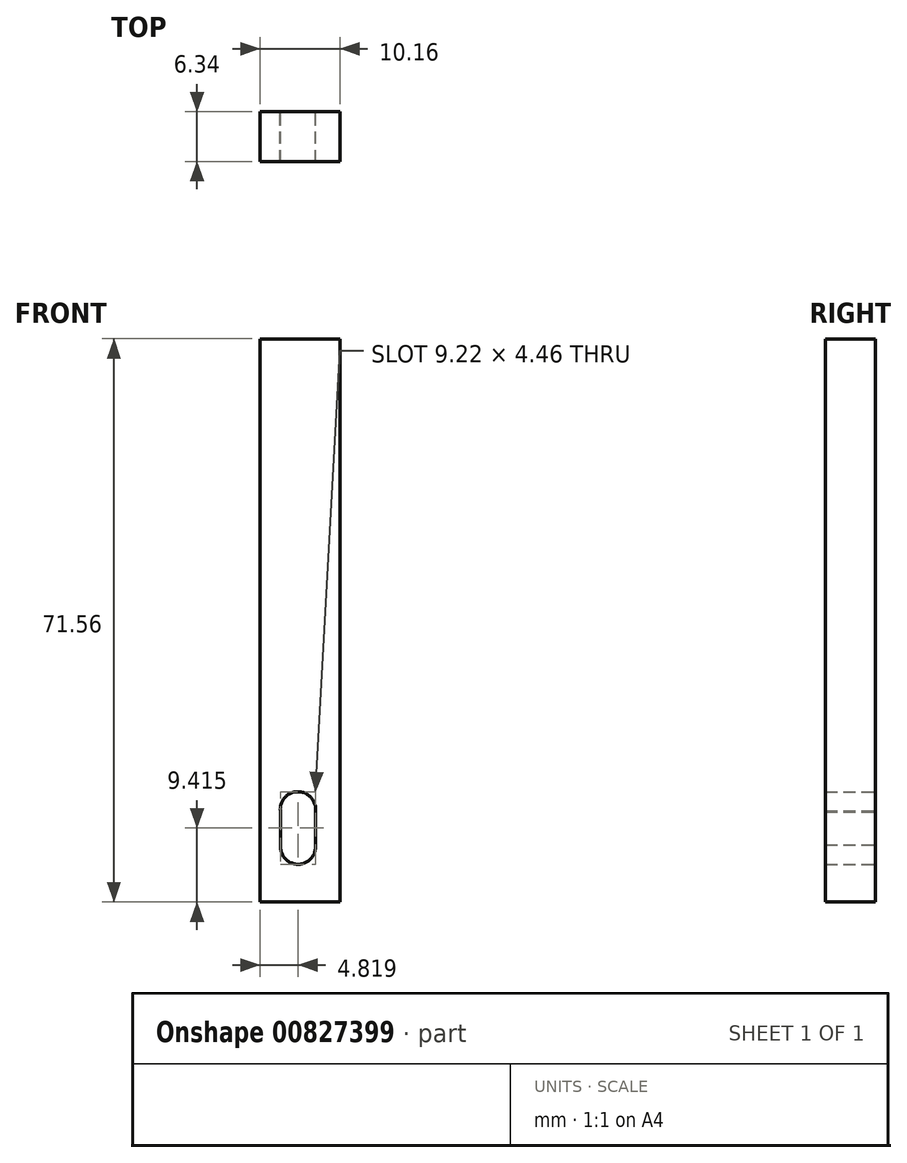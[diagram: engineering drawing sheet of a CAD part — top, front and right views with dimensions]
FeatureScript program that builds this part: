
annotation { "Feature Type Name" : "Feature", "Feature Type Description" : "" }
export const myFeature = defineFeature(function(context is Context, id is Id, definition is map)
    precondition{}
    {
        {
            var Q0;
            Q0=qCreatedBy(makeId("Front.planeOp"),FACE);
            var sketch = newSketch(context, id + "F0", { "sketchPlane" : qUnion([Q0])});
            skLineSegment(sketch, "E0.bottom", {"start": v(-5.08, 35.78) * mm, "end": v(5.08, 35.78) * mm});
            skLineSegment(sketch, "E0.top", {"start": v(-5.08, -35.78) * mm, "end": v(5.08, -35.78) * mm});
            skLineSegment(sketch, "E0.left", {"start": v(-5.08, 35.78) * mm, "end": v(-5.08, -35.78) * mm});
            skLineSegment(sketch, "E0.right", {"start": v(5.08, 35.78) * mm, "end": v(5.08, -35.78) * mm});
            skPoint(sketch, "E0.middle", {"position": v(0, 0) * mm});
            skArc(sketch, "E1", {"start": v(1.97, -24.22) * mm, "mid": v(-0.3, -21.76) * mm, "end": v(-2.49, -24.3) * mm});
            skLineSegment(sketch, "E2", {"start": v(-2.49, -24.3) * mm, "end": v(-2.49, -28.74) * mm});
            skLineSegment(sketch, "E3", {"start": v(1.97, -24.22) * mm, "end": v(1.97, -28.55) * mm});
            skArc(sketch, "E4", {"start": v(-2.49, -28.74) * mm, "mid": v(-0.16, -30.97) * mm, "end": v(1.97, -28.55) * mm});
            skSolve(sketch);
        }
        {
            var Q0;
            Q0=makeQuery(id+"F0.imprint","IMPRINT",FACE,{"disambiguationData":[TD([[makeQuery(id+"F0.imprint","IMPRINT",EDGE,{"derivedFrom":sQuery(id+"F0.wireOp",EDGE,"E0.bottom")}),-1.0]])]});
            extrude(context, id + "F1", {"entities" : qUnion([Q0]), "endBound" : BoundingType.SYMMETRIC, "depth" : 6.35 * mm, "offsetDistance" : 25.4 * mm});
        }
    });
